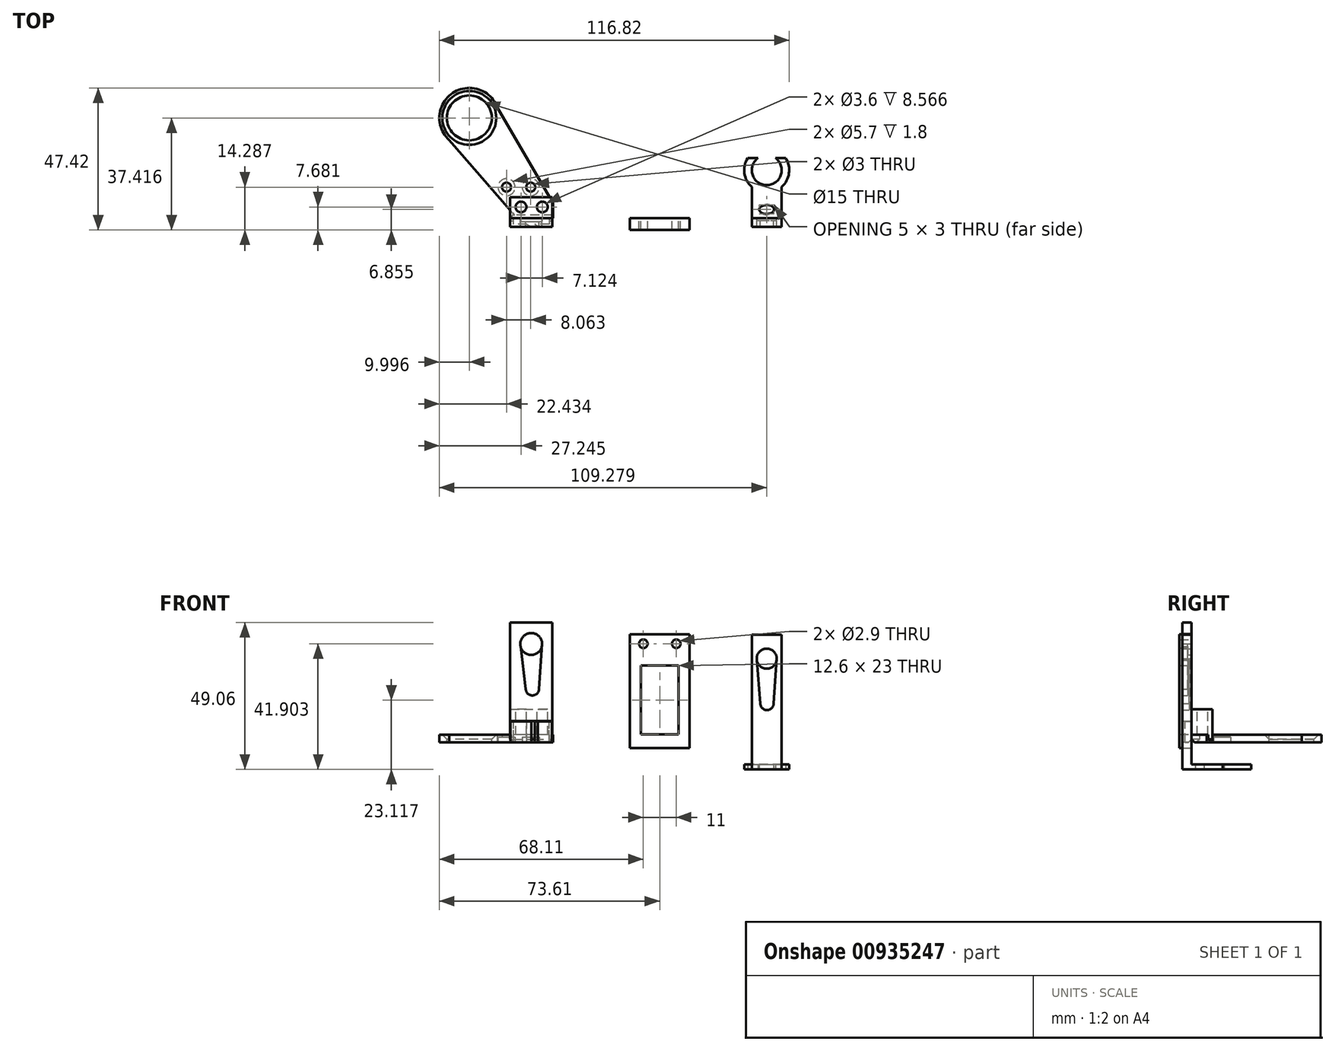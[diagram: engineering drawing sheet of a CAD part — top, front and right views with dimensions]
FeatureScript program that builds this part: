
annotation { "Feature Type Name" : "Feature", "Feature Type Description" : "" }
export const myFeature = defineFeature(function(context is Context, id is Id, definition is map)
    precondition{}
    {
        {
            var Q0;
            Q0=qCreatedBy(makeId("Front.planeOp"),FACE);
            var sketch = newSketch(context, id + "F0", { "sketchPlane" : qUnion([Q0])});
            skLineSegment(sketch, "E0.bottom", {"start": v(-10, 18.57) * mm, "end": v(10, 18.57) * mm});
            skLineSegment(sketch, "E0.top", {"start": v(-10, -19.43) * mm, "end": v(10, -19.43) * mm});
            skLineSegment(sketch, "E0.left", {"start": v(-10, 18.57) * mm, "end": v(-10, -19.43) * mm});
            skLineSegment(sketch, "E0.right", {"start": v(10, 18.57) * mm, "end": v(10, -19.43) * mm});
            skLineSegment(sketch, "E1.bottom", {"start": v(-6.3, 8.1) * mm, "end": v(6.3, 8.1) * mm});
            skLineSegment(sketch, "E1.top", {"start": v(-6.3, -14.9) * mm, "end": v(6.3, -14.9) * mm});
            skLineSegment(sketch, "E1.left", {"start": v(-6.3, 8.1) * mm, "end": v(-6.3, -14.9) * mm});
            skLineSegment(sketch, "E1.right", {"start": v(6.3, 8.1) * mm, "end": v(6.3, -14.9) * mm});
            skCircle(sketch, "E2", {"center": v(-5.5, 15.38) * mm, "radius": 1.45 * mm});
            skCircle(sketch, "E3.MirrorC", {"center": v(5.5, 15.38) * mm, "radius": 1.45 * mm});
            skSolve(sketch);
        }
        {
            var Q0;
            Q0 = qSketchRegion(id + "F0", true);
            extrude(context, id + "F1", {"entities" : qUnion([Q0]), "depth" : 4 * mm, "offsetDistance" : 25 * mm});
        }
        {
            var Q0;
            Q0=qCreatedBy(makeId("Front.planeOp"),FACE);
            var sketch = newSketch(context, id + "F2", { "sketchPlane" : qUnion([Q0])});
            skLineSegment(sketch, "E4.bottom", {"start": v(30.71, 18.48) * mm, "end": v(40.71, 18.48) * mm});
            skLineSegment(sketch, "E4.top", {"start": v(30.71, -26.52) * mm, "end": v(40.71, -26.52) * mm});
            skLineSegment(sketch, "E4.left", {"start": v(30.71, 18.48) * mm, "end": v(30.71, -26.52) * mm});
            skLineSegment(sketch, "E4.right", {"start": v(40.71, 18.48) * mm, "end": v(40.71, -26.52) * mm});
            skCircle(sketch, "E5", {"center": v(35.71, 10.43) * mm, "radius": 3.35 * mm});
            skPoint(sketch, "E5.centerSnap0", {"position": v(35.71, 18.48) * mm});
            skCircle(sketch, "E6", {"center": v(35.81, -4.57) * mm, "radius": 2.2 * mm});
            skLineSegment(sketch, "E7", {"start": v(32.36, 10.43) * mm, "end": v(33.61, -4.57) * mm});
            skLineSegment(sketch, "E8", {"start": v(33.61, -4.57) * mm, "end": v(38.01, -4.57) * mm});
            skLineSegment(sketch, "E9", {"start": v(38.01, -4.57) * mm, "end": v(39.07, 10.43) * mm});
            skLineSegment(sketch, "E10", {"start": v(39.07, 10.43) * mm, "end": v(32.36, 10.43) * mm});
            skLineSegment(sketch, "E11", {"start": v(30.71, -24.92) * mm, "end": v(40.71, -24.92) * mm});
            skSolve(sketch);
        }
        {
            var Q0;
            Q0 = qSketchRegion(id + "F2", true);
            extrude(context, id + "F3", {"entities" : qUnion([Q0]), "depth" : 3 * mm, "offsetDistance" : 25 * mm});
        }
        {
            var Q0;
            {var subQ0=sQuery(id+"F2.wireOp",EDGE,"E7");var subQ1=sQuery(id+"F2.wireOp",EDGE,"E5");var subQ2=makeQuery(id+"F2.imprint","INTERSECT",VERTEX,{"derivedFrom":[subQ1,subQ0]});Q0=makeQuery(id+"F2.imprint","IMPRINT",FACE,{"disambiguationData":[TD([[makeQuery(id+"F2.imprint","IMPRINT",EDGE,{"disambiguationData":[TD([[subQ2,-1.0]])],"derivedFrom":subQ1}),-1.0]])]});}
            var Q1;
            {var subQ0=sQuery(id+"F2.wireOp",EDGE,"E8");Q1=makeQuery(id+"F2.imprint","IMPRINT",FACE,{"disambiguationData":[TD([[makeQuery(id+"F2.imprint","IMPRINT",EDGE,{"derivedFrom":subQ0}),1.0]])]});}
            var Q2;
            {var subQ0=sQuery(id+"F2.wireOp",EDGE,"E8");Q2=makeQuery(id+"F2.imprint","IMPRINT",FACE,{"disambiguationData":[TD([[makeQuery(id+"F2.imprint","IMPRINT",EDGE,{"derivedFrom":subQ0}),-1.0]])]});}
            extrude(context, id + "F4", {"entities" : qUnion([Q0, Q1, Q2]), "operationType" : NewBodyOperationType.ADD, "depth" : 0.8 * mm, "offsetDistance" : 25 * mm});
        }
        {
            var Q0;
            {var subQ0=sQuery(id+"F2.wireOp",EDGE,"E4.top");Q0=makeQuery(id+"F2.imprint","IMPRINT",FACE,{"disambiguationData":[TD([[makeQuery(id+"F2.imprint","IMPRINT",EDGE,{"derivedFrom":subQ0}),1.0]])]});}
            extrude(context, id + "F5", {"entities" : qUnion([Q0]), "operationType" : NewBodyOperationType.ADD, "oppositeDirection" : true, "depth" : 20 * mm, "offsetDistance" : 25 * mm});
        }
        {
            var Q0;
            {var subQ0=sQuery(id+"F2.wireOp",EDGE,"E4.top");Q0=makeQuery(id+"F5.boolean.opBoolean","MERGE",FACE,{"derivedFrom":[makeQuery(id+"F3.opExtrude","SWEPT_FACE",FACE,{"disambiguationData":[OSD([subQ0])]}),makeQuery(id+"F5.opExtrude","SWEPT_FACE",FACE,{"disambiguationData":[OSD([subQ0])]})]});}
            var sketch = newSketch(context, id + "F6", { "sketchPlane" : qUnion([Q0])});
            skCircle(sketch, "E12", {"center": v(35.71, -15.98) * mm, "radius": 7.5 * mm});
            skCircle(sketch, "E13", {"center": v(35.71, -15.98) * mm, "radius": 5 * mm});
            skEllipse(sketch, "E14", {"center": v(35.67, -2.85) * mm, "majorRadius": 2.5 * mm, "minorRadius": 1.5 * mm, "majorAxis": v(-1, 0)});
            skLineSegment(sketch, "E15", {"start": v(42.05, -20) * mm, "end": v(29.38, -20) * mm});
            skSolve(sketch);
        }
        {
            var Q0;
            {var subQ0=sQuery(id+"F6.wireOp",EDGE,"E13");var subQ2=sQuery(id+"F2.wireOp",EDGE,"E4.top");var subQ5=makeQuery(id+"F5.opExtrude","CAP_EDGE",EDGE,{"disambiguationData":[OSD([subQ2])],"isStart":false});var subQ6=makeQuery(id+"F6.imprint","INTERSECT",VERTEX,{"disambiguationData":[OD(0.0)],"derivedFrom":[subQ5,subQ0]});Q0=makeQuery(id+"F6.imprint","IMPRINT",FACE,{"disambiguationData":[TD([[makeQuery(id+"F6.imprint","IMPRINT",EDGE,{"disambiguationData":[TD([[subQ6,1.0]])],"derivedFrom":subQ0}),-1.0]])]});}
            var Q1;
            {var subQ0=sQuery(id+"F6.wireOp",EDGE,"E13");var subQ2=sQuery(id+"F2.wireOp",EDGE,"E4.top");var subQ5=makeQuery(id+"F5.opExtrude","CAP_EDGE",EDGE,{"disambiguationData":[OSD([subQ2])],"isStart":false});var subQ6=makeQuery(id+"F6.imprint","INTERSECT",VERTEX,{"disambiguationData":[OD(1.0)],"derivedFrom":[subQ5,subQ0]});Q1=makeQuery(id+"F6.imprint","IMPRINT",FACE,{"disambiguationData":[TD([[makeQuery(id+"F6.imprint","IMPRINT",EDGE,{"disambiguationData":[TD([[subQ6,-1.0]])],"derivedFrom":subQ0}),-1.0]])]});}
            var Q2;
            {var subQ0=sQuery(id+"F6.wireOp",EDGE,"E12");var subQ1=sQuery(id+"F2.wireOp",EDGE,"E4.left");var subQ2=sQuery(id+"F2.wireOp",EDGE,"E4.top");var subQ3=makeQuery(id+"F5.boolean.opBoolean","MERGE",EDGE,{"derivedFrom":[makeQuery(id+"F3.opExtrude","SWEPT_EDGE",EDGE,{"disambiguationData":[OSD([subQ2,subQ1])]}),makeQuery(id+"F5.opExtrude","SWEPT_EDGE",EDGE,{"disambiguationData":[OSD([subQ2,subQ1])]})]});var subQ4=makeQuery(id+"F6.imprint","INTERSECT",VERTEX,{"derivedFrom":[subQ3,subQ0]});Q2=makeQuery(id+"F6.imprint","IMPRINT",FACE,{"disambiguationData":[TD([[makeQuery(id+"F6.imprint","IMPRINT",EDGE,{"disambiguationData":[TD([[subQ4,1.0]])],"derivedFrom":subQ0}),1.0]])]});}
            var Q3;
            {var subQ0=sQuery(id+"F6.wireOp",EDGE,"E15");var subQ1=sQuery(id+"F6.wireOp",EDGE,"E12");var subQ2=makeQuery(id+"F6.imprint","INTERSECT",VERTEX,{"disambiguationData":[OD(0.0)],"derivedFrom":[subQ1,subQ0]});Q3=makeQuery(id+"F6.imprint","IMPRINT",FACE,{"disambiguationData":[TD([[makeQuery(id+"F6.imprint","IMPRINT",EDGE,{"disambiguationData":[TD([[subQ2,-1.0]])],"derivedFrom":subQ1}),1.0]])]});}
            var Q4;
            {var subQ0=sQuery(id+"F6.wireOp",EDGE,"E15");var subQ1=sQuery(id+"F6.wireOp",EDGE,"E12");var subQ2=makeQuery(id+"F6.imprint","INTERSECT",VERTEX,{"disambiguationData":[OD(1.0)],"derivedFrom":[subQ1,subQ0]});Q4=makeQuery(id+"F6.imprint","IMPRINT",FACE,{"disambiguationData":[TD([[makeQuery(id+"F6.imprint","IMPRINT",EDGE,{"disambiguationData":[TD([[subQ2,1.0]])],"derivedFrom":subQ1}),1.0]])]});}
            extrude(context, id + "F7", {"entities" : qUnion([Q0, Q1, Q2, Q3, Q4]), "operationType" : NewBodyOperationType.ADD, "oppositeDirection" : true, "depth" : 1.6 * mm, "offsetDistance" : 25 * mm});
        }
        {
            var Q0;
            Q0=makeQuery(id+"F6.imprint","IMPRINT",FACE,{"disambiguationData":[TD([[makeQuery(id+"F6.imprint","IMPRINT",EDGE,{"derivedFrom":sQuery(id+"F6.wireOp",EDGE,"E14")}),1.0]])]});
            var Q1;
            {var subQ0=sQuery(id+"F6.wireOp",EDGE,"E13");var subQ6=sQuery(id+"F6.wireOp",EDGE,"E15");var subQ7=makeQuery(id+"F6.imprint","INTERSECT",VERTEX,{"disambiguationData":[OD(0.0)],"derivedFrom":[subQ0,subQ6]});Q1=makeQuery(id+"F6.imprint","IMPRINT",FACE,{"disambiguationData":[TD([[makeQuery(id+"F6.imprint","IMPRINT",EDGE,{"disambiguationData":[TD([[subQ7,-1.0]])],"derivedFrom":subQ6}),1.0]])]});}
            extrude(context, id + "F8", {"entities" : qUnion([Q0, Q1]), "operationType" : NewBodyOperationType.REMOVE, "oppositeDirection" : true, "depth" : 25 * mm, "offsetDistance" : 25 * mm});
        }
        {
            var Q0;
            Q0=qCreatedBy(makeId("Front.planeOp"),FACE);
            var sketch = newSketch(context, id + "F9", { "sketchPlane" : qUnion([Q0])});
            skLineSegment(sketch, "E16.bottom", {"start": v(-49.95, 22.54) * mm, "end": v(-35.95, 22.54) * mm});
            skLineSegment(sketch, "E16.top", {"start": v(-49.95, -17.46) * mm, "end": v(-35.95, -17.46) * mm});
            skLineSegment(sketch, "E16.left", {"start": v(-49.95, 22.54) * mm, "end": v(-49.95, -17.46) * mm});
            skLineSegment(sketch, "E16.right", {"start": v(-35.95, 22.54) * mm, "end": v(-35.95, -17.46) * mm});
            skCircle(sketch, "E17", {"center": v(-42.95, 15.32) * mm, "radius": 3.65 * mm});
            skPoint(sketch, "E17.centerSnap0", {"position": v(-42.95, 22.54) * mm});
            skCircle(sketch, "E18", {"center": v(-42.55, 0.32) * mm, "radius": 2.2 * mm});
            skLineSegment(sketch, "E19", {"start": v(-46.6, 15.32) * mm, "end": v(-44.75, 0.32) * mm});
            skLineSegment(sketch, "E20", {"start": v(-44.75, 0.32) * mm, "end": v(-40.35, 0.32) * mm});
            skLineSegment(sketch, "E21", {"start": v(-40.35, 0.32) * mm, "end": v(-39.3, 15.32) * mm});
            skLineSegment(sketch, "E22", {"start": v(-39.3, 15.32) * mm, "end": v(-46.6, 15.32) * mm});
            skLineSegment(sketch, "E23", {"start": v(-49.95, -15.46) * mm, "end": v(-35.95, -15.46) * mm});
            skLineSegment(sketch, "E24", {"start": v(-49.95, -6.43) * mm, "end": v(-35.95, -6.43) * mm});
            skLineSegment(sketch, "E25", {"start": v(-49.95, -10.43) * mm, "end": v(-35.95, -10.43) * mm});
            skSolve(sketch);
        }
        {
            var Q0;
            {var subQ12=sQuery(id+"F9.wireOp",EDGE,"E16.bottom");Q0=makeQuery(id+"F9.imprint","IMPRINT",FACE,{"disambiguationData":[TD([[makeQuery(id+"F9.imprint","IMPRINT",EDGE,{"derivedFrom":subQ12}),-1.0]])]});}
            extrude(context, id + "F10", {"entities" : qUnion([Q0]), "depth" : 3 * mm, "offsetDistance" : 25 * mm});
        }
        {
            var Q0;
            {var subQ0=sQuery(id+"F9.wireOp",EDGE,"E20");Q0=makeQuery(id+"F9.imprint","IMPRINT",FACE,{"disambiguationData":[TD([[makeQuery(id+"F9.imprint","IMPRINT",EDGE,{"derivedFrom":subQ0}),1.0]])]});}
            var Q1;
            {var subQ0=sQuery(id+"F9.wireOp",EDGE,"E20");Q1=makeQuery(id+"F9.imprint","IMPRINT",FACE,{"disambiguationData":[TD([[makeQuery(id+"F9.imprint","IMPRINT",EDGE,{"derivedFrom":subQ0}),-1.0]])]});}
            var Q2;
            {var subQ0=sQuery(id+"F9.wireOp",EDGE,"E19");var subQ1=sQuery(id+"F9.wireOp",EDGE,"E17");var subQ2=makeQuery(id+"F9.imprint","INTERSECT",VERTEX,{"derivedFrom":[subQ1,subQ0]});Q2=makeQuery(id+"F9.imprint","IMPRINT",FACE,{"disambiguationData":[TD([[makeQuery(id+"F9.imprint","IMPRINT",EDGE,{"disambiguationData":[TD([[subQ2,-1.0]])],"derivedFrom":subQ1}),-1.0]])]});}
            extrude(context, id + "F11", {"entities" : qUnion([Q0, Q1, Q2]), "operationType" : NewBodyOperationType.ADD, "depth" : 1.2 * mm, "offsetDistance" : 25 * mm});
        }
        {
            var Q0;
            {var subQ0=sQuery(id+"F9.wireOp",EDGE,"E23");Q0=makeQuery(id+"F9.imprint","IMPRINT",FACE,{"disambiguationData":[TD([[makeQuery(id+"F9.imprint","IMPRINT",EDGE,{"derivedFrom":subQ0}),1.0]])]});}
            var Q1;
            {var subQ0=sQuery(id+"F9.wireOp",EDGE,"E16.top");Q1=makeQuery(id+"F9.imprint","IMPRINT",FACE,{"disambiguationData":[TD([[makeQuery(id+"F9.imprint","IMPRINT",EDGE,{"derivedFrom":subQ0}),1.0]])]});}
            extrude(context, id + "F12", {"entities" : qUnion([Q0, Q1]), "oppositeDirection" : true, "depth" : 7 * mm, "offsetDistance" : 25 * mm});
        }
        {
            var Q0;
            {var subQ0=sQuery(id+"F9.wireOp",EDGE,"E24");Q0=makeQuery(id+"F9.imprint","IMPRINT",FACE,{"disambiguationData":[TD([[makeQuery(id+"F9.imprint","IMPRINT",EDGE,{"derivedFrom":subQ0}),-1.0]])]});}
            extrude(context, id + "F13", {"entities" : qUnion([Q0]), "operationType" : NewBodyOperationType.ADD, "depth" : 3 * mm, "offsetDistance" : 25 * mm, "hasSecondDirection" : true, "secondDirectionOppositeDirection" : true, "secondDirectionDepth" : 7 * mm});
        }
        {
            var Q0;
            Q0=makeQuery(id+"F13.opExtrude","SWEPT_FACE",FACE,{"disambiguationData":[OSD([sQuery(id+"F9.wireOp",EDGE,"E24")])]});
            var sketch = newSketch(context, id + "F14", { "sketchPlane" : qUnion([Q0])});
            skCircle(sketch, "E26", {"center": v(-39.24, 3.68) * mm, "radius": 1.8 * mm});
            skCircle(sketch, "E27", {"center": v(-46.36, 3.68) * mm, "radius": 1.8 * mm});
            skCircle(sketch, "E28", {"center": v(-39.24, 3.68) * mm, "radius": 1.45 * mm});
            skCircle(sketch, "E29", {"center": v(-46.36, 3.68) * mm, "radius": 1.45 * mm});
            skSolve(sketch);
        }
        {
            var Q0;
            Q0 = qSketchRegion(id + "F14", true);
            var Q1;
            Q1=makeQuery(id+"F14.imprint","IMPRINT",FACE,{"disambiguationData":[TD([[makeQuery(id+"F14.imprint","IMPRINT",EDGE,{"derivedFrom":sQuery(id+"F14.wireOp",EDGE,"E28")}),1.0]])]});
            var Q2;
            Q2=makeQuery(id+"F14.imprint","IMPRINT",FACE,{"disambiguationData":[TD([[makeQuery(id+"F14.imprint","IMPRINT",EDGE,{"derivedFrom":sQuery(id+"F14.wireOp",EDGE,"E29")}),1.0]])]});
            extrude(context, id + "F15", {"entities" : qUnion([Q0, Q1, Q2]), "operationType" : NewBodyOperationType.REMOVE, "oppositeDirection" : true, "depth" : 25 * mm, "offsetDistance" : 25 * mm});
        }
        {
            var Q0;
            Q0=makeQuery(id+"F14.imprint","IMPRINT",FACE,{"disambiguationData":[TD([[makeQuery(id+"F14.imprint","IMPRINT",EDGE,{"derivedFrom":sQuery(id+"F14.wireOp",EDGE,"E28")}),1.0]])]});
            var Q1;
            Q1=makeQuery(id+"F14.imprint","IMPRINT",FACE,{"disambiguationData":[TD([[makeQuery(id+"F14.imprint","IMPRINT",EDGE,{"derivedFrom":sQuery(id+"F14.wireOp",EDGE,"E29")}),1.0]])]});
            extrude(context, id + "F16", {"entities" : qUnion([Q0, Q1]), "operationType" : NewBodyOperationType.REMOVE, "oppositeDirection" : true, "depth" : 9 * mm, "offsetDistance" : 25 * mm});
        }
        {
            var Q0;
            Q0=qCreatedBy(makeId("Top.planeOp"),FACE);
            var sketch = newSketch(context, id + "F17", { "sketchPlane" : qUnion([Q0])});
            skCircle(sketch, "E30", {"center": v(-63.61, 33.42) * mm, "radius": 10 * mm});
            skCircle(sketch, "E31", {"center": v(-63.61, 33.42) * mm, "radius": 7.5 * mm});
            skLineSegment(sketch, "E32", {"start": v(-70.3, 25.97) * mm, "end": v(-47.67, 0) * mm});
            skLineSegment(sketch, "E33", {"start": v(-47.67, 0) * mm, "end": v(-35.67, 0) * mm});
            skLineSegment(sketch, "E34", {"start": v(-35.67, 0) * mm, "end": v(-35.67, 5.09) * mm});
            skLineSegment(sketch, "E35", {"start": v(-35.67, 5.09) * mm, "end": v(-54.2, 36.8) * mm});
            skSolve(sketch);
        }
        {
            var Q0;
            Q0 = qSketchRegion(id + "F17", true);
            extrude(context, id + "F18", {"entities" : qUnion([Q0]), "operationType" : NewBodyOperationType.ADD, "oppositeDirection" : true, "depth" : 17.5 * mm, "offsetDistance" : 25 * mm, "hasSecondDirection" : true, "secondDirectionOppositeDirection" : true, "secondDirectionDepth" : 15 * mm});
        }
        {
            var Q0;
            Q0=makeQuery(id+"F18.opExtrude","CAP_EDGE",EDGE,{"disambiguationData":[OSD([sQuery(id+"F17.wireOp",EDGE,"E31")])],"isStart":true});
            chamfer(context, id + "F19", {"entities" : qUnion([Q0]), "width" : 1.5 * mm, "tangentPropagation" : true});
        }
        {
            var Q0;
            Q0=makeQuery(id+"F12.opExtrude","SWEPT_EDGE",EDGE,{"disambiguationData":[OSD([sQuery(id+"F9.wireOp",EDGE,"E16.top"),sQuery(id+"F9.wireOp",EDGE,"E16.left")])]});
            var Q1;
            Q1=makeQuery(id+"F18.opExtrude","CAP_EDGE",EDGE,{"disambiguationData":[OSD([sQuery(id+"F17.wireOp",EDGE,"E33")])],"isStart":false});
            var Q2;
            Q2=makeQuery(id+"F12.opExtrude","SWEPT_EDGE",EDGE,{"disambiguationData":[OSD([sQuery(id+"F9.wireOp",EDGE,"E16.top"),sQuery(id+"F9.wireOp",EDGE,"E16.right")])]});
            chamfer(context, id + "F20", {"entities" : qUnion([Q0, Q1, Q2]), "width" : 1 * mm});
        }
        {
            var Q0;
            Q0=qCreatedBy(makeId("Top.planeOp"),FACE);
            var sketch = newSketch(context, id + "F21", { "sketchPlane" : qUnion([Q0])});
            skLineSegment(sketch, "E36", {"start": v(-49.92, 0) * mm, "end": v(-49.92, -3) * mm});
            skLineSegment(sketch, "E37", {"start": v(-49.92, -3) * mm, "end": v(-35.98, -3) * mm});
            skLineSegment(sketch, "E38", {"start": v(-35.98, -3) * mm, "end": v(-35.98, 0) * mm});
            skLineSegment(sketch, "E39", {"start": v(-35.98, 0) * mm, "end": v(-36.98, 0) * mm});
            skLineSegment(sketch, "E40", {"start": v(-36.98, 0) * mm, "end": v(-36.98, -2.14) * mm});
            skLineSegment(sketch, "E41", {"start": v(-36.98, -2.14) * mm, "end": v(-48.91, -2.14) * mm});
            skLineSegment(sketch, "E42", {"start": v(-48.91, -2.14) * mm, "end": v(-48.91, 0) * mm});
            skLineSegment(sketch, "E43", {"start": v(-48.91, 0) * mm, "end": v(-49.92, 0) * mm});
            skLineSegment(sketch, "E44", {"start": v(-44.36, -2.14) * mm, "end": v(-42.95, -3) * mm});
            skLineSegment(sketch, "E45", {"start": v(-42.95, -3) * mm, "end": v(-40.73, -3) * mm});
            skLineSegment(sketch, "E46", {"start": v(-40.73, -3) * mm, "end": v(-41.77, -2.14) * mm});
            skSolve(sketch);
        }
        {
            var Q0;
            {var subQ4=sQuery(id+"F21.wireOp",EDGE,"E36");Q0=makeQuery(id+"F21.imprint","IMPRINT",FACE,{"disambiguationData":[TD([[makeQuery(id+"F21.imprint","IMPRINT",EDGE,{"derivedFrom":subQ4}),1.0]])]});}
            var Q1;
            {var subQ1=sQuery(id+"F21.wireOp",EDGE,"E38");Q1=makeQuery(id+"F21.imprint","IMPRINT",FACE,{"disambiguationData":[TD([[makeQuery(id+"F21.imprint","IMPRINT",EDGE,{"derivedFrom":subQ1}),1.0]])]});}
            extrude(context, id + "F22", {"entities" : qUnion([Q0, Q1]), "operationType" : NewBodyOperationType.ADD, "oppositeDirection" : true, "depth" : 17.5 * mm, "offsetDistance" : 25 * mm, "hasSecondDirection" : true, "secondDirectionOppositeDirection" : true, "secondDirectionDepth" : 10.5 * mm});
        }
        {
            var Q0;
            Q0=makeQuery(id+"F22.opExtrude","CAP_EDGE",EDGE,{"disambiguationData":[OSD([sQuery(id+"F21.wireOp",EDGE,"E39")])],"isStart":false});
            var Q1;
            Q1=makeQuery(id+"F22.opExtrude","CAP_EDGE",EDGE,{"disambiguationData":[OSD([sQuery(id+"F21.wireOp",EDGE,"E43")])],"isStart":false});
            chamfer(context, id + "F23", {"entities" : qUnion([Q0, Q1]), "width" : 1 * mm});
        }
        {
            var Q0;
            Q0=makeQuery(id+"F18.opExtrude","CAP_FACE",FACE,{"disambiguationData":[OSD([sQuery(id+"F17.wireOp",EDGE,"E30"),sQuery(id+"F17.wireOp",EDGE,"E31"),sQuery(id+"F17.wireOp",EDGE,"E32"),sQuery(id+"F17.wireOp",EDGE,"E33"),sQuery(id+"F17.wireOp",EDGE,"E34"),sQuery(id+"F17.wireOp",EDGE,"E35")])],"isStart":false});
            var sketch = newSketch(context, id + "F24", { "sketchPlane" : qUnion([Q0])});
            skCircle(sketch, "E47", {"center": v(-51.18, -10.29) * mm, "radius": 2.85 * mm});
            skCircle(sketch, "E48", {"center": v(-51.18, -10.29) * mm, "radius": 1.5 * mm});
            skCircle(sketch, "E49", {"center": v(-43.11, -10.29) * mm, "radius": 2.85 * mm});
            skCircle(sketch, "E50", {"center": v(-43.11, -10.29) * mm, "radius": 1.5 * mm});
            skSolve(sketch);
        }
        {
            var Q0;
            Q0=makeQuery(id+"F24.imprint","IMPRINT",FACE,{"disambiguationData":[TD([[makeQuery(id+"F24.imprint","IMPRINT",EDGE,{"derivedFrom":sQuery(id+"F24.wireOp",EDGE,"E47")}),1.0]])]});
            var Q1;
            Q1=makeQuery(id+"F24.imprint","IMPRINT",FACE,{"disambiguationData":[TD([[makeQuery(id+"F24.imprint","IMPRINT",EDGE,{"derivedFrom":sQuery(id+"F24.wireOp",EDGE,"E49")}),1.0]])]});
            extrude(context, id + "F25", {"entities" : qUnion([Q0, Q1]), "operationType" : NewBodyOperationType.REMOVE, "oppositeDirection" : true, "depth" : 1.8 * mm, "offsetDistance" : 25 * mm});
        }
        {
            var Q0;
            Q0=makeQuery(id+"F24.imprint","IMPRINT",FACE,{"disambiguationData":[TD([[makeQuery(id+"F24.imprint","IMPRINT",EDGE,{"derivedFrom":sQuery(id+"F24.wireOp",EDGE,"E48")}),1.0]])]});
            var Q1;
            Q1=makeQuery(id+"F24.imprint","IMPRINT",FACE,{"disambiguationData":[TD([[makeQuery(id+"F24.imprint","IMPRINT",EDGE,{"derivedFrom":sQuery(id+"F24.wireOp",EDGE,"E50")}),1.0]])]});
            extrude(context, id + "F26", {"entities" : qUnion([Q0, Q1]), "operationType" : NewBodyOperationType.REMOVE, "oppositeDirection" : true, "depth" : 25 * mm, "offsetDistance" : 25 * mm});
        }
    });
